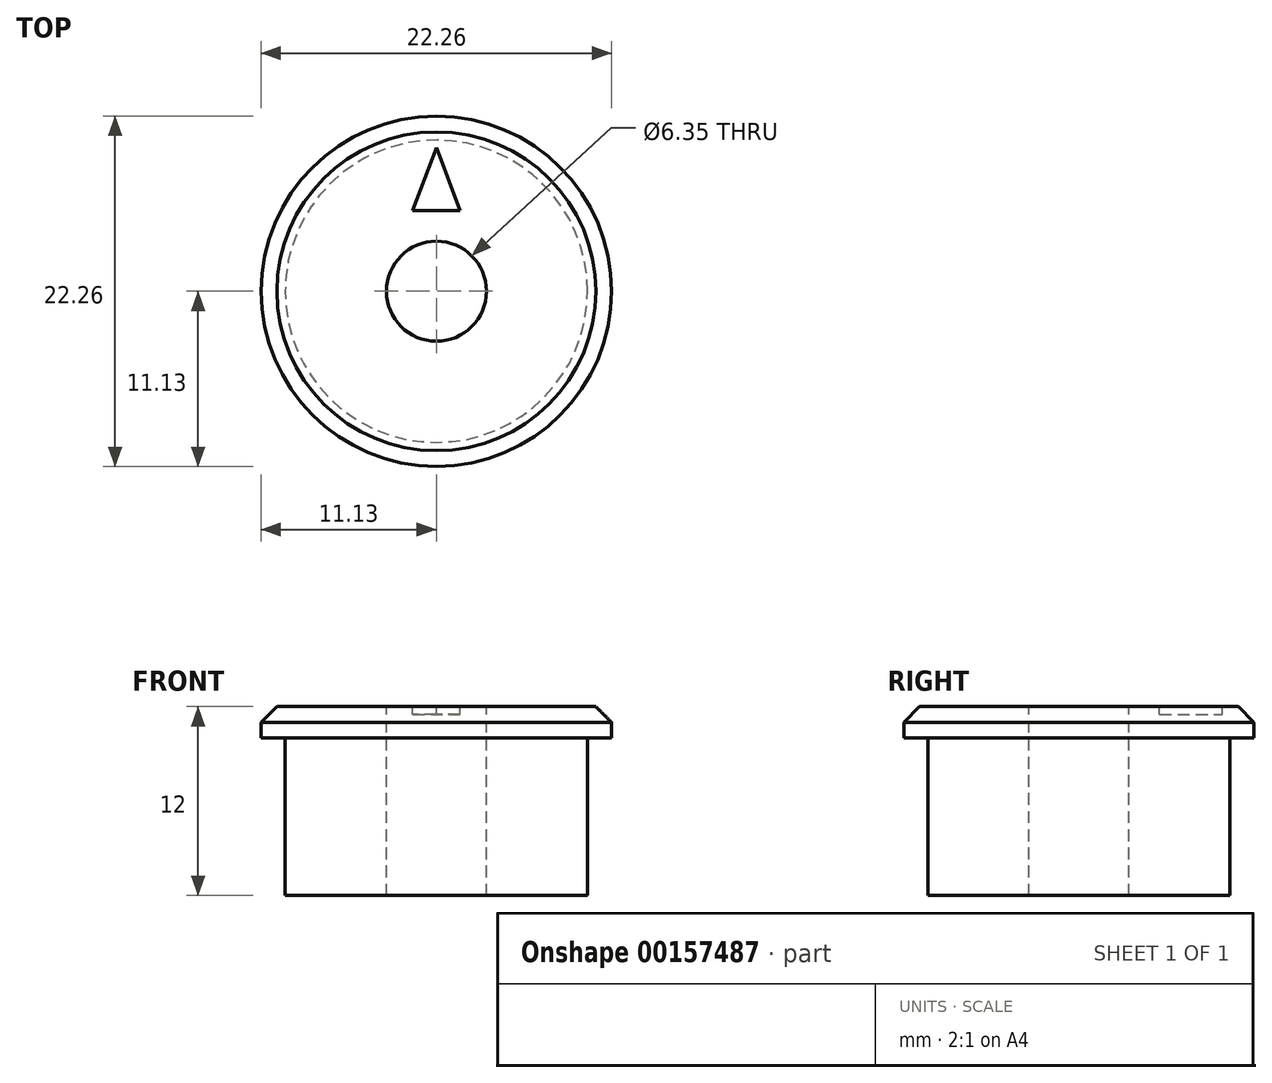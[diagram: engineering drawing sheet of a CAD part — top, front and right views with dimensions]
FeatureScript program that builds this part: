
annotation { "Feature Type Name" : "Feature", "Feature Type Description" : "" }
export const myFeature = defineFeature(function(context is Context, id is Id, definition is map)
    precondition{}
    {
        {
            var Q0;
            Q0=qCreatedBy(makeId("Top.planeOp"),FACE);
            var sketch = newSketch(context, id + "F0", { "sketchPlane" : qUnion([Q0])});
            skCircle(sketch, "E0", {"center": v(0, 0) * mm, "radius": 9.6 * mm});
            skSolve(sketch);
        }
        {
            var Q0;
            Q0 = qSketchRegion(id + "F0", true);
            extrude(context, id + "F1", {"entities" : qUnion([Q0]), "oppositeDirection" : true, "depth" : 10 * mm});
        }
        {
            var Q0;
            Q0=makeQuery(id+"F1.opExtrude","CAP_FACE",FACE,{"disambiguationData":[OSD([sQuery(id+"F0.wireOp",EDGE,"E0")])],"isStart":true});
            var sketch = newSketch(context, id + "F2", { "sketchPlane" : qUnion([Q0])});
            skCircle(sketch, "E1", {"center": v(0, 0) * mm, "radius": 6.6 * mm});
            skSolve(sketch);
        }
        {
            var Q0;
            Q0=makeQuery(id+"F1.opExtrude","CAP_FACE",FACE,{"disambiguationData":[OSD([sQuery(id+"F0.wireOp",EDGE,"E0")])],"isStart":true});
            var sketch = newSketch(context, id + "F3", { "sketchPlane" : qUnion([Q0])});
            skCircle(sketch, "E2", {"center": v(0, 0) * mm, "radius": 11.12 * mm});
            skSolve(sketch);
        }
        {
            var Q0;
            Q0 = qSketchRegion(id + "F3", true);
            extrude(context, id + "F4", {"entities" : qUnion([Q0]), "operationType" : NewBodyOperationType.ADD, "depth" : 2 * mm});
        }
        {
            var Q0;
            Q0=makeQuery(id+"F4.opExtrude","CAP_EDGE",EDGE,{"disambiguationData":[OSD([sQuery(id+"F3.wireOp",EDGE,"E2")])],"isStart":false});
            chamfer(context, id + "F5", {"entities" : qUnion([Q0]), "width" : 1 * mm, "tangentPropagation" : true});
        }
        {
            var Q0;
            Q0=makeQuery(id+"F4.opExtrude","CAP_FACE",FACE,{"disambiguationData":[OSD([sQuery(id+"F3.wireOp",EDGE,"E2")])],"isStart":false});
            var sketch = newSketch(context, id + "F6", { "sketchPlane" : qUnion([Q0])});
            skCircle(sketch, "E3", {"center": v(0, 0) * mm, "radius": 3.17 * mm});
            skSolve(sketch);
        }
        {
            var Q0;
            Q0 = qSketchRegion(id + "F6", true);
            extrude(context, id + "F7", {"entities" : qUnion([Q0]), "operationType" : NewBodyOperationType.REMOVE, "endBound" : BoundingType.THROUGH_ALL, "oppositeDirection" : true, "depth" : 25 * mm});
        }
        {
            var Q0;
            Q0=makeQuery(id+"F4.opExtrude","CAP_FACE",FACE,{"disambiguationData":[OSD([sQuery(id+"F3.wireOp",EDGE,"E2")])],"isStart":false});
            var sketch = newSketch(context, id + "F8", { "sketchPlane" : qUnion([Q0])});
            skLineSegment(sketch, "E4", {"start": v(0, 9.12) * mm, "end": v(-1.5, 5.12) * mm});
            skLineSegment(sketch, "E5", {"start": v(-1.5, 5.12) * mm, "end": v(1.5, 5.12) * mm});
            skLineSegment(sketch, "E6", {"start": v(1.5, 5.12) * mm, "end": v(0, 9.12) * mm});
            skSolve(sketch);
        }
        {
            var Q0;
            Q0 = qSketchRegion(id + "F8", true);
            extrude(context, id + "F9", {"entities" : qUnion([Q0]), "operationType" : NewBodyOperationType.REMOVE, "oppositeDirection" : true, "depth" : 0.5 * mm});
        }
    });
